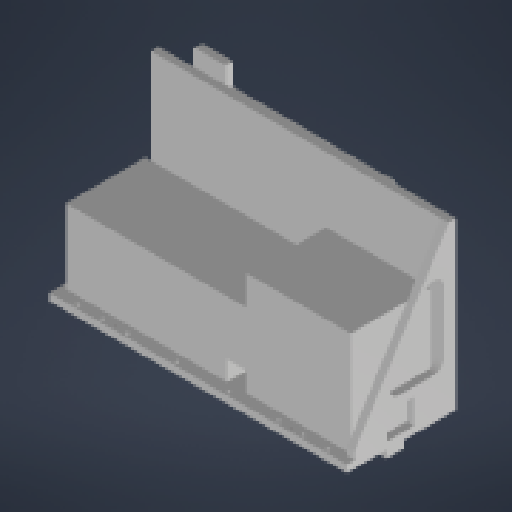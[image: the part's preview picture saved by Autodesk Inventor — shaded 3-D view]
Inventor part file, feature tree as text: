
AUTODESK INVENTOR PART (.ipt)
format: ipt  version: 2025 (Build 290162000, 162)  size: 306,688 bytes
history: native  units: in
note: dims shown in document units (in); Inventor stores cm internally (conversion verified against a paired STEP export)
features: hole x2, sketch x1
ambient origin geometry x8: Origin, YZ Plane, XZ Plane, XY Plane, X Axis, Y Axis, Z Axis, Center Point
bodies: Solid1 (feature_tree), Body1 (feature_tree)
feature tree (3):
  sketch  "Sketch1"  dims[d2=0.1969in d3=0.1969in d4=1.2008in d5=0.5906in d6=0.1969in d7=1.9685in d8=0.1969in d9=0.9843in d10=0.1969in d11=0.9843in d12=1.9488in d13=0.5906in d14=0.1969in d15=3.9173in d16=0.1969in d17=4.9016in d18=0.9843in d19=0.1969in d20=0.9843in d35=0.1936in d36=0.4724in d37=0.1575in d38=0.0787in d39=90.0deg d40=0.315in d41=0.0in d42=0.2559in d43=0.4724in d44=0.1575in d45=0.0787in d46=90.0deg d47=0.315in d48=0.0in d49=0.1969in d50=3.937in d51=0.1969in d52=3.937in d21=0.0394in d22=0.0394in d23=0.0394in d24=0.0059in d25=0.0098in d26=0.0148in d27=32.2835in d28=0.0295in d29=46.4567in d30=0.0025in d31=0.0295in d32=0.0148in d33=0.0148in d34=32.2835in]
  hole  "Hole3"  [1 undecoded]
  hole  "Hole4"  [1 undecoded]
note: 2 required parameter values undecoded (feature->parameter linkage not recoverable at this tier; creation-order binding heuristic only, values carry confidence <= 0.55)
